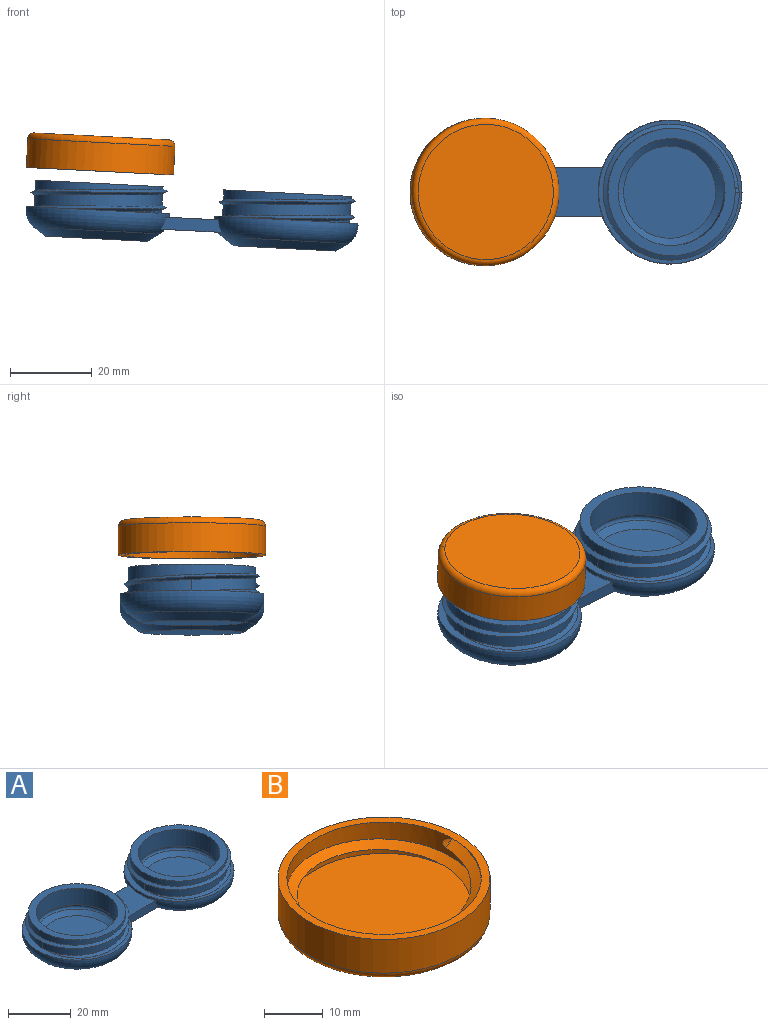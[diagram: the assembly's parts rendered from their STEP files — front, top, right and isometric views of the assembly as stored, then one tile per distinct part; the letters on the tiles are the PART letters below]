
ASSEMBLY  parts=2 mates=1
PART A: 40 faces, bbox 84.2x38.2x13.7 mm
  f0: cylinder r=15.55mm len=31.11mm, axis (0,0,-1), area 381mm2, adj f1,f21,f30,f31,f37,f38,f39
  f1: cylinder r=15.55mm len=31.11mm, axis (0,0,-1), area 95.8mm2, adj f0,f7,f30,f31
  f2: cylinder r=15.55mm len=31.11mm, axis (0,0,-1), area 381mm2, adj f3,f26,f32,f33,f34,f35,f36
  f3: cylinder r=15.55mm len=31.11mm, axis (0,0,-1), area 95.8mm2, adj f2,f12,f32,f33
  f4: plane 25x25mm, normal (0,0,-1), area 490.9mm2, adj f5
  f5: cone r=12.5mm half-angle=55.5deg, axis (0,0,1), area 309.6mm2, adj f4,f6
  f6: torus R=12.58mm, axis (0,0,1), area 570.3mm2, adj f5,f7,f8,f9,f10,f11,f18,f19
  f7: plane 35.2x35.2mm, normal (0,0,1), area 186.5mm2, adj f1,f6,f30,f31
  f8: plane 14.75x3.15mm, normal (0,-1,0), area 40.8mm2, adj f6,f11,f13,f17,f18,f19
  f9: plane 14.75x3.15mm, normal (0,1,0), area 40.8mm2, adj f6,f10,f13,f16,f18,f19
  f10: plane 0.7x0.36mm, normal (-1,0,0), area 0.1mm2, adj f6,f9,f18
  f11: plane 0.7x0.36mm, normal (-1,0,0), area 0.1mm2, adj f6,f8,f18
  f12: plane 35.2x35.2mm, normal (0,0,1), area 186.5mm2, adj f3,f13,f32,f33
  f13: torus R=12.58mm, axis (0,0,1), area 570.3mm2, adj f8,f9,f12,f14,f16,f17,f18,f19
  f14: cone r=12.5mm half-angle=55.5deg, axis (0,0,1), area 309.6mm2, adj f13,f15
  f15: plane 25x25mm, normal (0,0,-1), area 490.9mm2, adj f14
  f16: plane 0.7x0.36mm, normal (1,0,0), area 0.1mm2, adj f9,f13,f18
  f17: plane 0.7x0.36mm, normal (1,0,0), area 0.1mm2, adj f8,f13,f18
  f18: plane 14.6x12mm, normal (0,0,-1), area 162.7mm2, adj f6,f8,f9,f10,f11,f13,f16,f17
  f19: plane 12.96x12mm, normal (0,0,1), area 138.5mm2, adj f6,f8,f9,f13
  f20: cylinder r=13.05mm len=26.11mm, axis (0,0,-1), area 533.1mm2, adj f21,f24
  f21: plane 31.11x31.11mm, normal (0,0,1), area 224.7mm2, adj f0,f20
  f22: plane 22.52x22.52mm, normal (0,0,1), area 398.2mm2, adj f23
  f23: cone r=10.23mm half-angle=55.5deg, axis (0,0,1), area 175.5mm2, adj f22,f24
  f24: torus R=12.58mm, axis (0,0,1), area 172.2mm2, adj f20,f23
  f25: cylinder r=13.05mm len=26.11mm, axis (0,0,-1), area 533.1mm2, adj f26,f29
  f26: plane 31.11x31.11mm, normal (0,0,1), area 224.7mm2, adj f2,f25
  f27: plane 22.52x22.52mm, normal (0,0,1), area 398.2mm2, adj f28
  f28: cone r=10.23mm half-angle=55.5deg, axis (0,0,1), area 175.5mm2, adj f27,f29
  f29: torus R=12.58mm, axis (0,0,1), area 172.2mm2, adj f25,f28
  f30: bspline ~37.02x37.01mm, area 172.7mm2, adj f0,f1,f7,f31,f39
  f31: bspline ~37.02x37.01mm, area 154.8mm2, adj f0,f1,f7,f30,f38
  f32: bspline ~37.02x37.01mm, area 172.7mm2, adj f2,f3,f12,f33,f36
  f33: bspline ~37.02x37.01mm, area 154.8mm2, adj f2,f3,f12,f32,f35
  f34: plane 1.08x0.94mm, normal (-1,0,0), area 0.5mm2, adj f2,f35,f36
  f35: cone r=1.04mm half-angle=60deg, axis (0,0,1), area 1mm2, adj f2,f33,f34,f36
  f36: cone r=0mm half-angle=60deg, axis (0,0,-1), area 1mm2, adj f2,f32,f34,f35
  f37: plane 1.08x0.94mm, normal (-1,0,0), area 0.5mm2, adj f0,f38,f39
  f38: cone r=1.04mm half-angle=60deg, axis (0,0,1), area 1mm2, adj f0,f31,f37,f39
  f39: cone r=0mm half-angle=60deg, axis (0,0,-1), area 1mm2, adj f0,f30,f37,f38
PART B: 10 faces, bbox 39.8x39.8x9.3 mm
  f0: cylinder r=16.5mm len=33mm, axis (0,0,-1), area 387mm2, adj f2,f4,f6,f7,f8,f9
  f1: cylinder r=18mm len=36mm, axis (0,0,-1), area 791.7mm2, adj f2,f5
  f2: plane 36x36mm, normal (0,0,1), area 162.6mm2, adj f0,f1
  f3: plane 33x33mm, normal (0,0,-1), area 855.3mm2, adj f5
  f4: plane 33.01x33mm, normal (0,0,1), area 812mm2, adj f0,f6,f7
  f5: torus R=16.5mm, axis (0,0,1), area 258.4mm2, adj f1,f3
  f6: bspline ~38.11x33mm, area 295.3mm2, adj f0,f4,f7,f9
  f7: bspline ~38.11x33mm, area 245.3mm2, adj f0,f4,f6,f8
  f8: cone r=1.73mm half-angle=60deg, axis (0,0,1), area 3.6mm2, adj f0,f7,f9
  f9: cone r=0mm half-angle=60deg, axis (0,0,-1), area 2.7mm2, adj f0,f6,f8
PLACE A rot(axis=(0,1,0),2.9deg) t=(-14.44,-4.32,14.18)mm
PLACE B rot(axis=(0,-1,0),177.1deg) t=(-36.59,-4.32,31.34)mm
MATE planar B.f1 <-> A.f20  axis (-0.05,0,-1) through (-36.57,-4.32,31.84)mm
